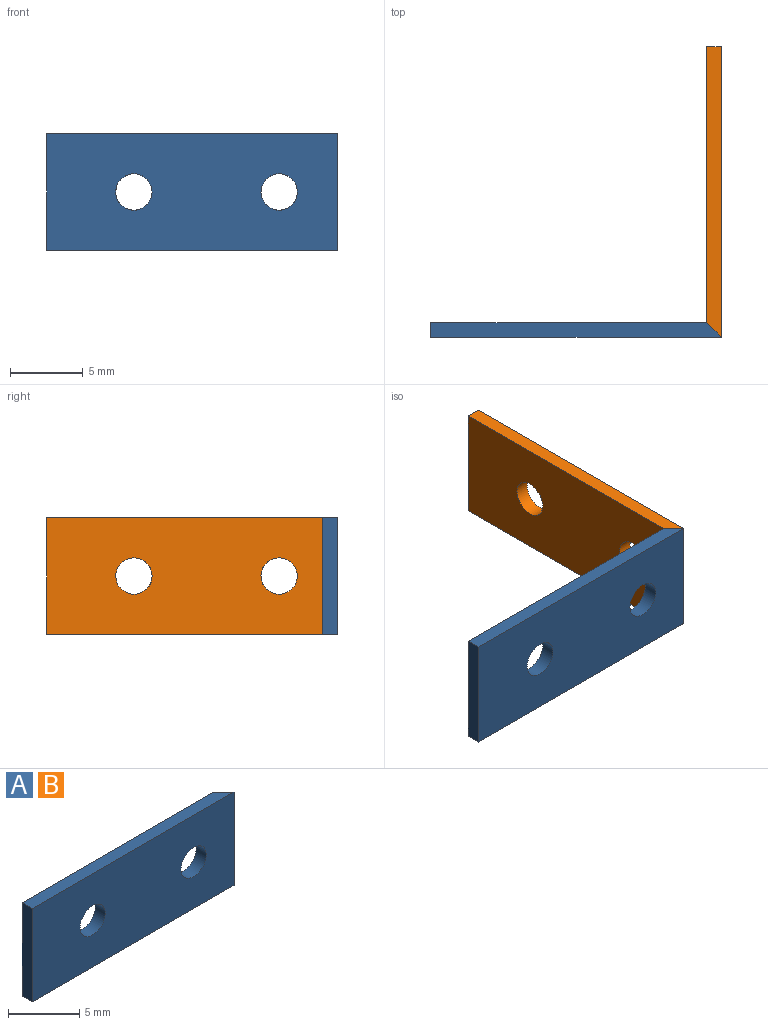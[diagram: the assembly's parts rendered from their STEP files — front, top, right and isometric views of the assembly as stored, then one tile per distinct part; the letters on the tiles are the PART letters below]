
ASSEMBLY  parts=2 mates=1
PART A: 8 faces, bbox 20x1x8 mm
  f0: plane 20x1mm, normal (0,0,1), area 19.5mm2, adj f1,f3,f4,f5
  f1: plane 19x8mm, normal (0,1,0), area 142.2mm2, adj f0,f2,f3,f5,f6,f7
  f2: plane 20x1mm, normal (0,0,-1), area 19.5mm2, adj f1,f3,f4,f5
  f3: plane 8x1mm, normal (-1,0,0), area 8mm2, adj f0,f1,f2,f4
  f4: plane 20x8mm, normal (0,-1,0), area 150.2mm2, adj f0,f2,f3,f5,f6,f7
  f5: plane 8x1mm, normal (0.71,0.71,0), area 11.3mm2, adj f0,f1,f2,f4
  f6: cylinder r=1.25mm len=2.5mm, axis (0,1,0), area 7.9mm2, adj f1,f4
  f7: cylinder r=1.25mm len=2.5mm, axis (0,1,0), area 7.9mm2, adj f1,f4
PART B: same geometry as A
PLACE A t=(-23.41,-21.44,-0.97)mm
PLACE B rot(axis=(-0.71,0.71,0),180deg) t=(15.59,17.56,-80.27)mm
MATE fastened A.f5 <-> B.f5  axis (0.71,0.71,0) through (16.09,-21.94,-40.62)mm
